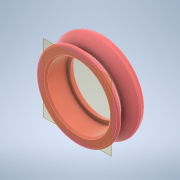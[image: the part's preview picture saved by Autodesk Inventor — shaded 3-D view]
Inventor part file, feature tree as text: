
AUTODESK INVENTOR PART (.ipt)
format: ipt  version: 2022 (Build 260153000, 153)  size: 382,464 bytes
history: native  units: in
note: dims shown in document units (in); Inventor stores cm internally (conversion verified against a paired STEP export)
features: other x2, plane x1, revolve x1, fillet x1, chamfer x1, sketch x1
ambient origin geometry x8: Origin, YZ Plane, XZ Plane, XY Plane, X Axis, Y Axis, Z Axis, Center Point
bodies: Solid1 (feature_tree)
feature tree (7):
  plane  "Work Plane1"
  revolve  "Revolution1"  [1 undecoded]
  fillet  "Fillet1"  [1 undecoded]
  chamfer  "Chamfer1"  Angle=45.0deg  [1 undecoded]
  sketch  "Sketch1"  dims[d0=0.876in d1=0.2756in d3=45.0deg d4=45.0deg d6=0.481in d7=0.0787in d8=0.748in d9=0.481in d10=90.0deg d11=0.0236in d12=0.0236in d13=0.125in d14=45.0deg d16=0.0394in d17=1.2244in]
  other  "<userpath>\Documents\CAD\guardSwerve1\Assembly1.iam"
  other  "Assembly1.iam"
note: 3 required parameter values undecoded (feature->parameter linkage not recoverable at this tier; creation-order binding heuristic only, values carry confidence <= 0.55)